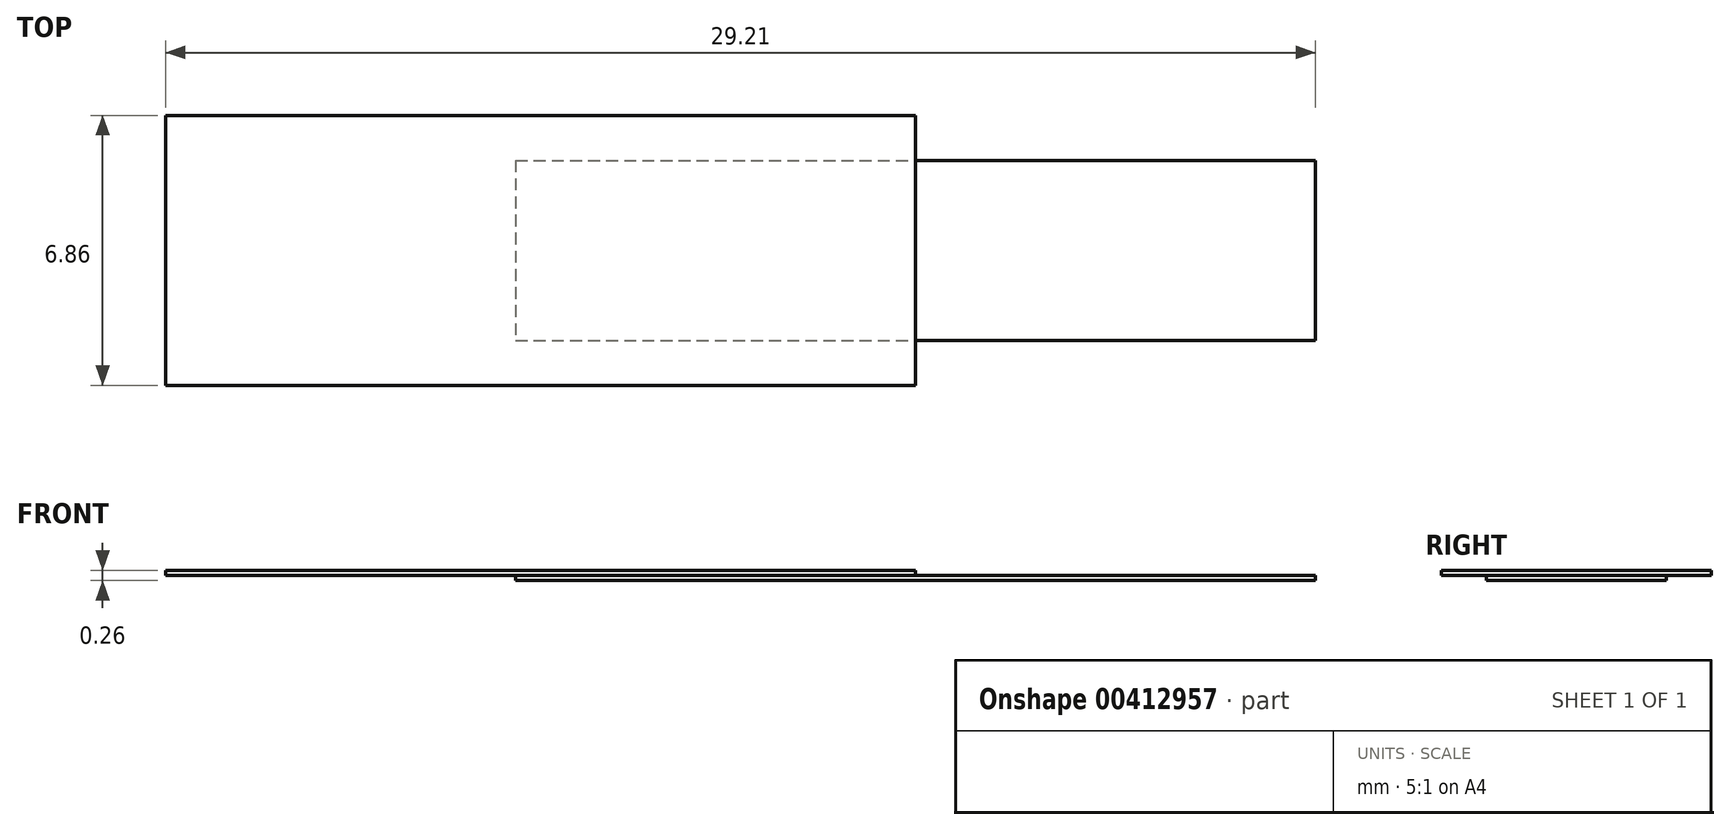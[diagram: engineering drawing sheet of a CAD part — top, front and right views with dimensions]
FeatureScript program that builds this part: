
annotation { "Feature Type Name" : "Feature", "Feature Type Description" : "" }
export const myFeature = defineFeature(function(context is Context, id is Id, definition is map)
    precondition{}
    {
        {
            var Q0;
            Q0=qCreatedBy(makeId("Top.planeOp"),FACE);
            var sketch = newSketch(context, id + "F0", { "sketchPlane" : qUnion([Q0])});
            skLineSegment(sketch, "E0.bottom", {"start": v(-41.56, -37.24) * mm, "end": v(-22.5, -37.24) * mm});
            skLineSegment(sketch, "E0.top", {"start": v(-41.56, -44.1) * mm, "end": v(-22.5, -44.1) * mm});
            skLineSegment(sketch, "E0.left", {"start": v(-41.56, -37.24) * mm, "end": v(-41.56, -44.1) * mm});
            skLineSegment(sketch, "E0.right", {"start": v(-22.5, -37.24) * mm, "end": v(-22.5, -44.1) * mm});
            skLineSegment(sketch, "E1.bottom", {"start": v(-32.67, -38.38) * mm, "end": v(-12.35, -38.38) * mm});
            skLineSegment(sketch, "E1.top", {"start": v(-32.67, -42.96) * mm, "end": v(-12.35, -42.96) * mm});
            skLineSegment(sketch, "E1.left", {"start": v(-32.67, -38.38) * mm, "end": v(-32.67, -42.96) * mm});
            skLineSegment(sketch, "E1.right", {"start": v(-12.35, -38.38) * mm, "end": v(-12.35, -42.96) * mm});
            skSolve(sketch);
        }
        {
            var Q0;
            {var subQ1=sQuery(id+"F0.wireOp",EDGE,"E0.bottom");Q0=makeQuery(id+"F0.imprint","IMPRINT",FACE,{"disambiguationData":[TD([[makeQuery(id+"F0.imprint","IMPRINT",EDGE,{"derivedFrom":subQ1}),-1.0]])]});}
            var Q1;
            {var subQ5=sQuery(id+"F0.wireOp",EDGE,"E1.left");Q1=makeQuery(id+"F0.imprint","IMPRINT",FACE,{"disambiguationData":[TD([[makeQuery(id+"F0.imprint","IMPRINT",EDGE,{"derivedFrom":subQ5}),1.0]])]});}
            extrude(context, id + "F1", {"entities" : qUnion([Q0, Q1]), "depth" : 0.13 * mm});
        }
        {
            var Q0;
            {var subQ5=sQuery(id+"F0.wireOp",EDGE,"E1.left");Q0=makeQuery(id+"F0.imprint","IMPRINT",FACE,{"disambiguationData":[TD([[makeQuery(id+"F0.imprint","IMPRINT",EDGE,{"derivedFrom":subQ5}),1.0]])]});}
            var Q1;
            {var subQ5=sQuery(id+"F0.wireOp",EDGE,"E1.right");Q1=makeQuery(id+"F0.imprint","IMPRINT",FACE,{"disambiguationData":[TD([[makeQuery(id+"F0.imprint","IMPRINT",EDGE,{"derivedFrom":subQ5}),-1.0]])]});}
            extrude(context, id + "F2", {"entities" : qUnion([Q0, Q1]), "oppositeDirection" : true, "depth" : 0.13 * mm});
        }
    });
